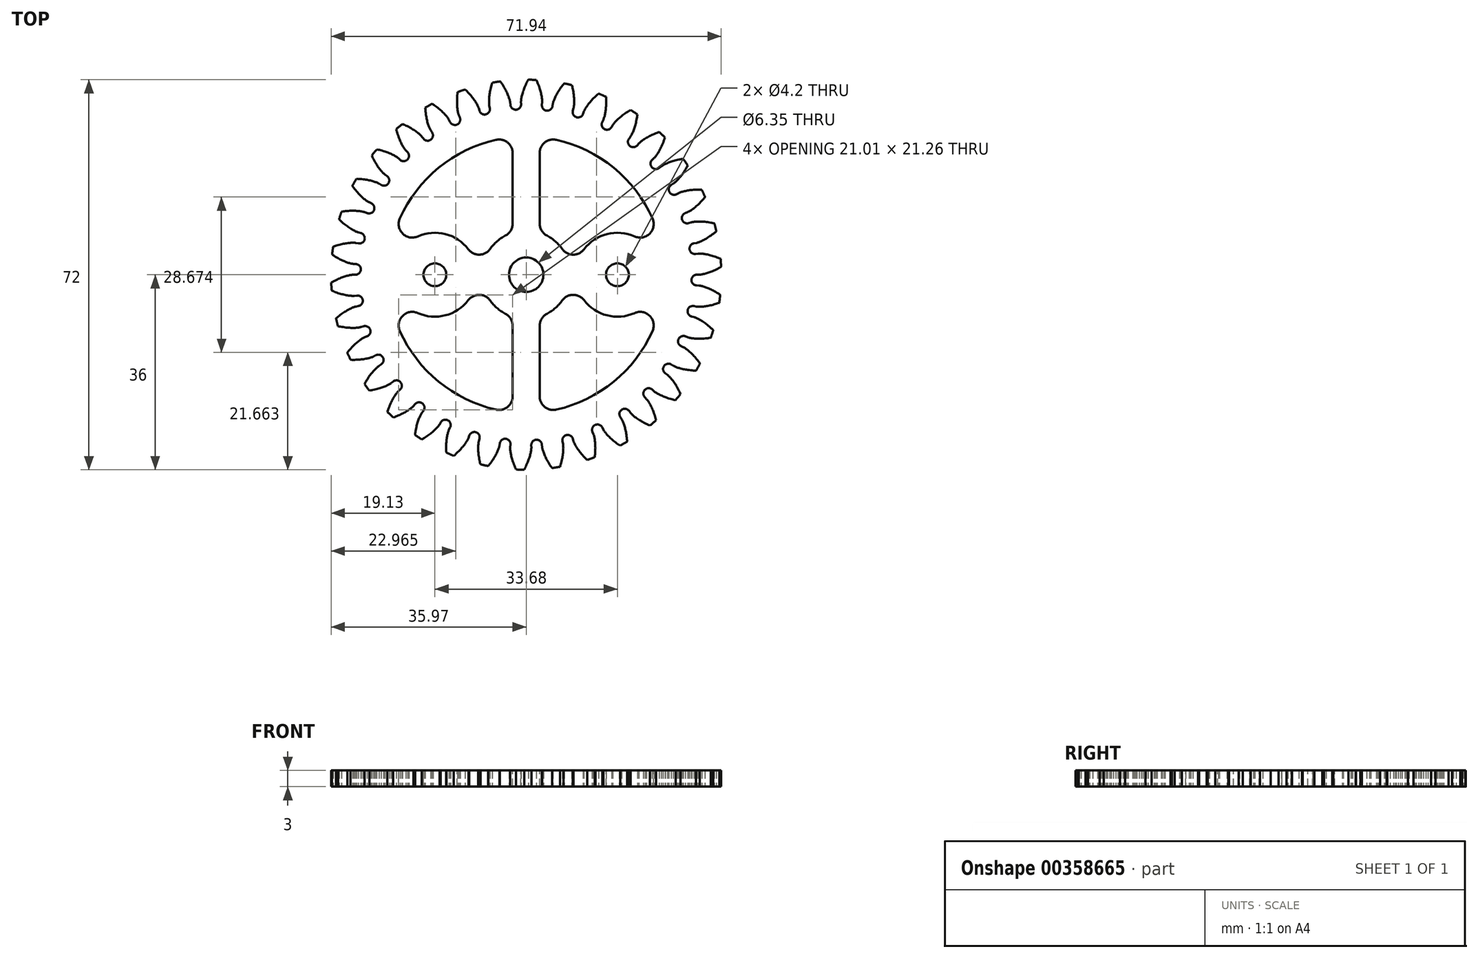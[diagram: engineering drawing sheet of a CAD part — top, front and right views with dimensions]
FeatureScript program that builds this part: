
annotation { "Feature Type Name" : "Feature", "Feature Type Description" : "" }
export const myFeature = defineFeature(function(context is Context, id is Id, definition is map)
    precondition{}
    {
        {
            assignVariable(context, id + "F0", {"name" : "T", "anyValue" : 34});
        }
        {
            assignVariable(context, id + "F1", {"name" : "SP", "anyValue" : 4});
        }
        {
            assignVariable(context, id + "F2", {"name" : "SF", "anyValue" : 2.5});
        }
        {
            var Q0;
            Q0=qCreatedBy(makeId("Top.planeOp"),FACE);
            var sketch = newSketch(context, id + "F3", { "sketchPlane" : qUnion([Q0])});
            skCircle(sketch, "E0", {"center": v(0, 0) * mm, "radius": 36 * mm});
            skCircle(sketch, "E1", {"center": v(0, 0) * mm, "radius": 34 * mm, "construction": true});
            skCircle(sketch, "E2", {"center": v(0, 0) * mm, "radius": 31.95 * mm, "construction": true});
            skCircle(sketch, "E3", {"center": v(0, 0) * mm, "radius": 31.5 * mm});
            skLineSegment(sketch, "E4", {"start": v(0, 0) * mm, "end": v(31.95, 0) * mm});
            skFitSpline(sketch, "E5", {"points": [v(31.95, 0) * mm, v(32, 0) * mm, v(32.14, 0.01) * mm, v(32.37, 0.05) * mm, v(32.7, 0.1) * mm, v(33.11, 0.21) * mm, v(33.61, 0.37) * mm, v(34.2, 0.58) * mm, v(34.85, 0.87) * mm, v(35.57, 1.23) * mm, v(36.35, 1.68) * mm], "startDerivative": vector(4.26, 0.15) * mm, "endDerivative": vector(16.12, 9.2) * mm});
            skLineSegment(sketch, "E6", {"start": v(0, 0) * mm, "end": v(35.98, -1.13) * mm, "construction": true});
            skLineSegment(sketch, "E7", {"start": v(0, 0) * mm, "end": v(34, 0.5) * mm, "construction": true});
            skFitSpline(sketch, "E8.MirrorCS", {"points": [v(31.89, -2) * mm, v(31.93, -2) * mm, v(32.08, -2.02) * mm, v(32.3, -2.07) * mm, v(32.63, -2.15) * mm, v(33.04, -2.28) * mm, v(33.52, -2.47) * mm, v(34.09, -2.72) * mm, v(34.72, -3.04) * mm, v(35.42, -3.45) * mm, v(36.18, -3.94) * mm], "startDerivative": vector(4.24, -0.42) * mm, "endDerivative": vector(15.51, -10.19) * mm});
            skLineSegment(sketch, "E9", {"start": v(0, 0) * mm, "end": v(31.89, -2) * mm});
            skSolve(sketch);
        }
        {
            var Q0;
            Q0=qCreatedBy(makeId("Top.planeOp"),FACE);
            var sketch = newSketch(context, id + "F4", { "sketchPlane" : qUnion([Q0])});
            skCircle(sketch, "E10", {"center": v(0, 0) * mm, "radius": 36 * mm});
            skSolve(sketch);
        }
        {
            var Q0;
            {var subQ0=sQuery(id+"F3.wireOp",EDGE,"E5");var subQ7=sQuery(id+"F3.wireOp",EDGE,"E0");var subQ8=makeQuery(id+"F3.imprint","INTERSECT",VERTEX,{"derivedFrom":[subQ7,subQ0]});Q0=makeQuery(id+"F3.imprint","IMPRINT",FACE,{"disambiguationData":[TD([[makeQuery(id+"F3.imprint","IMPRINT",EDGE,{"disambiguationData":[TD([[subQ8,1.0]])],"derivedFrom":subQ7}),1.0]])]});}
            extrude(context, id + "F5", {"entities" : qUnion([Q0]), "depth" : 6 * mm});
        }
        {
            var Q0;
            Q0=makeQuery(id+"F5.opExtrude","CAP_FACE",FACE,{"disambiguationData":[OSD([sQuery(id+"F3.wireOp",EDGE,"E0"),sQuery(id+"F3.wireOp",EDGE,"E3"),sQuery(id+"F3.wireOp",EDGE,"E4"),sQuery(id+"F3.wireOp",EDGE,"E5"),sQuery(id+"F3.wireOp",EDGE,"E8.MirrorCS"),sQuery(id+"F3.wireOp",EDGE,"E9")])],"isStart":true});
            var sketch = newSketch(context, id + "F6", { "sketchPlane" : qUnion([Q0])});
            skCircle(sketch, "E11", {"center": v(31.48, 0.99) * mm, "radius": 0.99 * mm});
            skSolve(sketch);
        }
        {
            var Q0;
            {var subQ1=makeQuery(id+"F5.opExtrude","CAP_EDGE",EDGE,{"disambiguationData":[OSD([sQuery(id+"F3.wireOp",EDGE,"E3")])],"isStart":true});Q0=makeQuery(id+"F6.imprint","IMPRINT",FACE,{"disambiguationData":[TD([[makeQuery(id+"F6.imprint","IMPRINT",EDGE,{"derivedFrom":subQ1}),-1.0]])]});}
            extrude(context, id + "F7", {"entities" : qUnion([Q0]), "operationType" : NewBodyOperationType.ADD, "oppositeDirection" : true, "depth" : 6 * mm});
        }
        {
            var Q0;
            Q0=makeQuery(id+"F4.imprint","IMPRINT",FACE,{"disambiguationData":[TD([[makeQuery(id+"F4.imprint","IMPRINT",EDGE,{"derivedFrom":sQuery(id+"F4.wireOp",EDGE,"E10")}),1.0]])]});
            extrude(context, id + "F8", {"entities" : qUnion([Q0]), "depth" : 3 * mm, "offsetDistance" : 25 * mm});
        }
        {
            var Q0;
            Q0=makeQuery(id+"F5.opExtrude","SWEPT_BODY",BODY,{"disambiguationData":[OSD([sQuery(id+"F3.wireOp",EDGE,"E0"),sQuery(id+"F3.wireOp",EDGE,"E3"),sQuery(id+"F3.wireOp",EDGE,"E4"),sQuery(id+"F3.wireOp",EDGE,"E5"),sQuery(id+"F3.wireOp",EDGE,"E8.MirrorCS"),sQuery(id+"F3.wireOp",EDGE,"E9")])]});
            var Q1;
            Q1=makeQuery(id+"F8.opExtrude","CAP_EDGE",EDGE,{"disambiguationData":[OSD([sQuery(id+"F4.wireOp",EDGE,"E10")])],"isStart":false});
            circularPattern(context, id + "F9", {"entities" : qUnion([Q0]), "axis" : qUnion([Q1]), "angle" : 360 * degree, "instanceCount" : getVariable(context, 'T'), "equalSpace" : true});
        }
        {
            var Q0;
            Q0=makeQuery(id+"F9.opPattern","COPY",BODY,{"derivedFrom":makeQuery(id+"F5.opExtrude","SWEPT_BODY",BODY,{"disambiguationData":[OSD([sQuery(id+"F3.wireOp",EDGE,"E0"),sQuery(id+"F3.wireOp",EDGE,"E3"),sQuery(id+"F3.wireOp",EDGE,"E4"),sQuery(id+"F3.wireOp",EDGE,"E5"),sQuery(id+"F3.wireOp",EDGE,"E8.MirrorCS"),sQuery(id+"F3.wireOp",EDGE,"E9")])]}),"instanceName":"5"});
            var Q1;
            Q1=makeQuery(id+"F9.opPattern","COPY",BODY,{"derivedFrom":makeQuery(id+"F5.opExtrude","SWEPT_BODY",BODY,{"disambiguationData":[OSD([sQuery(id+"F3.wireOp",EDGE,"E0"),sQuery(id+"F3.wireOp",EDGE,"E3"),sQuery(id+"F3.wireOp",EDGE,"E4"),sQuery(id+"F3.wireOp",EDGE,"E5"),sQuery(id+"F3.wireOp",EDGE,"E8.MirrorCS"),sQuery(id+"F3.wireOp",EDGE,"E9")])]}),"instanceName":"6"});
            var Q2;
            Q2=makeQuery(id+"F9.opPattern","COPY",BODY,{"derivedFrom":makeQuery(id+"F5.opExtrude","SWEPT_BODY",BODY,{"disambiguationData":[OSD([sQuery(id+"F3.wireOp",EDGE,"E0"),sQuery(id+"F3.wireOp",EDGE,"E3"),sQuery(id+"F3.wireOp",EDGE,"E4"),sQuery(id+"F3.wireOp",EDGE,"E5"),sQuery(id+"F3.wireOp",EDGE,"E8.MirrorCS"),sQuery(id+"F3.wireOp",EDGE,"E9")])]}),"instanceName":"7"});
            var Q3;
            Q3=makeQuery(id+"F9.opPattern","COPY",BODY,{"derivedFrom":makeQuery(id+"F5.opExtrude","SWEPT_BODY",BODY,{"disambiguationData":[OSD([sQuery(id+"F3.wireOp",EDGE,"E0"),sQuery(id+"F3.wireOp",EDGE,"E3"),sQuery(id+"F3.wireOp",EDGE,"E4"),sQuery(id+"F3.wireOp",EDGE,"E5"),sQuery(id+"F3.wireOp",EDGE,"E8.MirrorCS"),sQuery(id+"F3.wireOp",EDGE,"E9")])]}),"instanceName":"8"});
            var Q4;
            Q4=makeQuery(id+"F9.opPattern","COPY",BODY,{"derivedFrom":makeQuery(id+"F5.opExtrude","SWEPT_BODY",BODY,{"disambiguationData":[OSD([sQuery(id+"F3.wireOp",EDGE,"E0"),sQuery(id+"F3.wireOp",EDGE,"E3"),sQuery(id+"F3.wireOp",EDGE,"E4"),sQuery(id+"F3.wireOp",EDGE,"E5"),sQuery(id+"F3.wireOp",EDGE,"E8.MirrorCS"),sQuery(id+"F3.wireOp",EDGE,"E9")])]}),"instanceName":"9"});
            var Q5;
            Q5=makeQuery(id+"F9.opPattern","COPY",BODY,{"derivedFrom":makeQuery(id+"F5.opExtrude","SWEPT_BODY",BODY,{"disambiguationData":[OSD([sQuery(id+"F3.wireOp",EDGE,"E0"),sQuery(id+"F3.wireOp",EDGE,"E3"),sQuery(id+"F3.wireOp",EDGE,"E4"),sQuery(id+"F3.wireOp",EDGE,"E5"),sQuery(id+"F3.wireOp",EDGE,"E8.MirrorCS"),sQuery(id+"F3.wireOp",EDGE,"E9")])]}),"instanceName":"10"});
            var Q6;
            Q6=makeQuery(id+"F9.opPattern","COPY",BODY,{"derivedFrom":makeQuery(id+"F5.opExtrude","SWEPT_BODY",BODY,{"disambiguationData":[OSD([sQuery(id+"F3.wireOp",EDGE,"E0"),sQuery(id+"F3.wireOp",EDGE,"E3"),sQuery(id+"F3.wireOp",EDGE,"E4"),sQuery(id+"F3.wireOp",EDGE,"E5"),sQuery(id+"F3.wireOp",EDGE,"E8.MirrorCS"),sQuery(id+"F3.wireOp",EDGE,"E9")])]}),"instanceName":"11"});
            var Q7;
            Q7=makeQuery(id+"F9.opPattern","COPY",BODY,{"derivedFrom":makeQuery(id+"F5.opExtrude","SWEPT_BODY",BODY,{"disambiguationData":[OSD([sQuery(id+"F3.wireOp",EDGE,"E0"),sQuery(id+"F3.wireOp",EDGE,"E3"),sQuery(id+"F3.wireOp",EDGE,"E4"),sQuery(id+"F3.wireOp",EDGE,"E5"),sQuery(id+"F3.wireOp",EDGE,"E8.MirrorCS"),sQuery(id+"F3.wireOp",EDGE,"E9")])]}),"instanceName":"12"});
            var Q8;
            Q8=makeQuery(id+"F9.opPattern","COPY",BODY,{"derivedFrom":makeQuery(id+"F5.opExtrude","SWEPT_BODY",BODY,{"disambiguationData":[OSD([sQuery(id+"F3.wireOp",EDGE,"E0"),sQuery(id+"F3.wireOp",EDGE,"E3"),sQuery(id+"F3.wireOp",EDGE,"E4"),sQuery(id+"F3.wireOp",EDGE,"E5"),sQuery(id+"F3.wireOp",EDGE,"E8.MirrorCS"),sQuery(id+"F3.wireOp",EDGE,"E9")])]}),"instanceName":"13"});
            var Q9;
            Q9=makeQuery(id+"F9.opPattern","COPY",BODY,{"derivedFrom":makeQuery(id+"F5.opExtrude","SWEPT_BODY",BODY,{"disambiguationData":[OSD([sQuery(id+"F3.wireOp",EDGE,"E0"),sQuery(id+"F3.wireOp",EDGE,"E3"),sQuery(id+"F3.wireOp",EDGE,"E4"),sQuery(id+"F3.wireOp",EDGE,"E5"),sQuery(id+"F3.wireOp",EDGE,"E8.MirrorCS"),sQuery(id+"F3.wireOp",EDGE,"E9")])]}),"instanceName":"14"});
            var Q10;
            Q10=makeQuery(id+"F9.opPattern","COPY",BODY,{"derivedFrom":makeQuery(id+"F5.opExtrude","SWEPT_BODY",BODY,{"disambiguationData":[OSD([sQuery(id+"F3.wireOp",EDGE,"E0"),sQuery(id+"F3.wireOp",EDGE,"E3"),sQuery(id+"F3.wireOp",EDGE,"E4"),sQuery(id+"F3.wireOp",EDGE,"E5"),sQuery(id+"F3.wireOp",EDGE,"E8.MirrorCS"),sQuery(id+"F3.wireOp",EDGE,"E9")])]}),"instanceName":"15"});
            var Q11;
            Q11=makeQuery(id+"F9.opPattern","COPY",BODY,{"derivedFrom":makeQuery(id+"F5.opExtrude","SWEPT_BODY",BODY,{"disambiguationData":[OSD([sQuery(id+"F3.wireOp",EDGE,"E0"),sQuery(id+"F3.wireOp",EDGE,"E3"),sQuery(id+"F3.wireOp",EDGE,"E4"),sQuery(id+"F3.wireOp",EDGE,"E5"),sQuery(id+"F3.wireOp",EDGE,"E8.MirrorCS"),sQuery(id+"F3.wireOp",EDGE,"E9")])]}),"instanceName":"16"});
            var Q12;
            Q12=makeQuery(id+"F9.opPattern","COPY",BODY,{"derivedFrom":makeQuery(id+"F5.opExtrude","SWEPT_BODY",BODY,{"disambiguationData":[OSD([sQuery(id+"F3.wireOp",EDGE,"E0"),sQuery(id+"F3.wireOp",EDGE,"E3"),sQuery(id+"F3.wireOp",EDGE,"E4"),sQuery(id+"F3.wireOp",EDGE,"E5"),sQuery(id+"F3.wireOp",EDGE,"E8.MirrorCS"),sQuery(id+"F3.wireOp",EDGE,"E9")])]}),"instanceName":"17"});
            var Q13;
            Q13=makeQuery(id+"F9.opPattern","COPY",BODY,{"derivedFrom":makeQuery(id+"F5.opExtrude","SWEPT_BODY",BODY,{"disambiguationData":[OSD([sQuery(id+"F3.wireOp",EDGE,"E0"),sQuery(id+"F3.wireOp",EDGE,"E3"),sQuery(id+"F3.wireOp",EDGE,"E4"),sQuery(id+"F3.wireOp",EDGE,"E5"),sQuery(id+"F3.wireOp",EDGE,"E8.MirrorCS"),sQuery(id+"F3.wireOp",EDGE,"E9")])]}),"instanceName":"18"});
            var Q14;
            Q14=makeQuery(id+"F9.opPattern","COPY",BODY,{"derivedFrom":makeQuery(id+"F5.opExtrude","SWEPT_BODY",BODY,{"disambiguationData":[OSD([sQuery(id+"F3.wireOp",EDGE,"E0"),sQuery(id+"F3.wireOp",EDGE,"E3"),sQuery(id+"F3.wireOp",EDGE,"E4"),sQuery(id+"F3.wireOp",EDGE,"E5"),sQuery(id+"F3.wireOp",EDGE,"E8.MirrorCS"),sQuery(id+"F3.wireOp",EDGE,"E9")])]}),"instanceName":"19"});
            var Q15;
            Q15=makeQuery(id+"F9.opPattern","COPY",BODY,{"derivedFrom":makeQuery(id+"F5.opExtrude","SWEPT_BODY",BODY,{"disambiguationData":[OSD([sQuery(id+"F3.wireOp",EDGE,"E0"),sQuery(id+"F3.wireOp",EDGE,"E3"),sQuery(id+"F3.wireOp",EDGE,"E4"),sQuery(id+"F3.wireOp",EDGE,"E5"),sQuery(id+"F3.wireOp",EDGE,"E8.MirrorCS"),sQuery(id+"F3.wireOp",EDGE,"E9")])]}),"instanceName":"20"});
            var Q16;
            Q16=makeQuery(id+"F9.opPattern","COPY",BODY,{"derivedFrom":makeQuery(id+"F5.opExtrude","SWEPT_BODY",BODY,{"disambiguationData":[OSD([sQuery(id+"F3.wireOp",EDGE,"E0"),sQuery(id+"F3.wireOp",EDGE,"E3"),sQuery(id+"F3.wireOp",EDGE,"E4"),sQuery(id+"F3.wireOp",EDGE,"E5"),sQuery(id+"F3.wireOp",EDGE,"E8.MirrorCS"),sQuery(id+"F3.wireOp",EDGE,"E9")])]}),"instanceName":"21"});
            var Q17;
            Q17=makeQuery(id+"F9.opPattern","COPY",BODY,{"derivedFrom":makeQuery(id+"F5.opExtrude","SWEPT_BODY",BODY,{"disambiguationData":[OSD([sQuery(id+"F3.wireOp",EDGE,"E0"),sQuery(id+"F3.wireOp",EDGE,"E3"),sQuery(id+"F3.wireOp",EDGE,"E4"),sQuery(id+"F3.wireOp",EDGE,"E5"),sQuery(id+"F3.wireOp",EDGE,"E8.MirrorCS"),sQuery(id+"F3.wireOp",EDGE,"E9")])]}),"instanceName":"22"});
            var Q18;
            Q18=makeQuery(id+"F9.opPattern","COPY",BODY,{"derivedFrom":makeQuery(id+"F5.opExtrude","SWEPT_BODY",BODY,{"disambiguationData":[OSD([sQuery(id+"F3.wireOp",EDGE,"E0"),sQuery(id+"F3.wireOp",EDGE,"E3"),sQuery(id+"F3.wireOp",EDGE,"E4"),sQuery(id+"F3.wireOp",EDGE,"E5"),sQuery(id+"F3.wireOp",EDGE,"E8.MirrorCS"),sQuery(id+"F3.wireOp",EDGE,"E9")])]}),"instanceName":"23"});
            var Q19;
            Q19=makeQuery(id+"F9.opPattern","COPY",BODY,{"derivedFrom":makeQuery(id+"F5.opExtrude","SWEPT_BODY",BODY,{"disambiguationData":[OSD([sQuery(id+"F3.wireOp",EDGE,"E0"),sQuery(id+"F3.wireOp",EDGE,"E3"),sQuery(id+"F3.wireOp",EDGE,"E4"),sQuery(id+"F3.wireOp",EDGE,"E5"),sQuery(id+"F3.wireOp",EDGE,"E8.MirrorCS"),sQuery(id+"F3.wireOp",EDGE,"E9")])]}),"instanceName":"24"});
            var Q20;
            Q20=makeQuery(id+"F9.opPattern","COPY",BODY,{"derivedFrom":makeQuery(id+"F5.opExtrude","SWEPT_BODY",BODY,{"disambiguationData":[OSD([sQuery(id+"F3.wireOp",EDGE,"E0"),sQuery(id+"F3.wireOp",EDGE,"E3"),sQuery(id+"F3.wireOp",EDGE,"E4"),sQuery(id+"F3.wireOp",EDGE,"E5"),sQuery(id+"F3.wireOp",EDGE,"E8.MirrorCS"),sQuery(id+"F3.wireOp",EDGE,"E9")])]}),"instanceName":"25"});
            var Q21;
            Q21=makeQuery(id+"F9.opPattern","COPY",BODY,{"derivedFrom":makeQuery(id+"F5.opExtrude","SWEPT_BODY",BODY,{"disambiguationData":[OSD([sQuery(id+"F3.wireOp",EDGE,"E0"),sQuery(id+"F3.wireOp",EDGE,"E3"),sQuery(id+"F3.wireOp",EDGE,"E4"),sQuery(id+"F3.wireOp",EDGE,"E5"),sQuery(id+"F3.wireOp",EDGE,"E8.MirrorCS"),sQuery(id+"F3.wireOp",EDGE,"E9")])]}),"instanceName":"26"});
            var Q22;
            Q22=makeQuery(id+"F9.opPattern","COPY",BODY,{"derivedFrom":makeQuery(id+"F5.opExtrude","SWEPT_BODY",BODY,{"disambiguationData":[OSD([sQuery(id+"F3.wireOp",EDGE,"E0"),sQuery(id+"F3.wireOp",EDGE,"E3"),sQuery(id+"F3.wireOp",EDGE,"E4"),sQuery(id+"F3.wireOp",EDGE,"E5"),sQuery(id+"F3.wireOp",EDGE,"E8.MirrorCS"),sQuery(id+"F3.wireOp",EDGE,"E9")])]}),"instanceName":"27"});
            var Q23;
            Q23=makeQuery(id+"F9.opPattern","COPY",BODY,{"derivedFrom":makeQuery(id+"F5.opExtrude","SWEPT_BODY",BODY,{"disambiguationData":[OSD([sQuery(id+"F3.wireOp",EDGE,"E0"),sQuery(id+"F3.wireOp",EDGE,"E3"),sQuery(id+"F3.wireOp",EDGE,"E4"),sQuery(id+"F3.wireOp",EDGE,"E5"),sQuery(id+"F3.wireOp",EDGE,"E8.MirrorCS"),sQuery(id+"F3.wireOp",EDGE,"E9")])]}),"instanceName":"28"});
            var Q24;
            Q24=makeQuery(id+"F9.opPattern","COPY",BODY,{"derivedFrom":makeQuery(id+"F5.opExtrude","SWEPT_BODY",BODY,{"disambiguationData":[OSD([sQuery(id+"F3.wireOp",EDGE,"E0"),sQuery(id+"F3.wireOp",EDGE,"E3"),sQuery(id+"F3.wireOp",EDGE,"E4"),sQuery(id+"F3.wireOp",EDGE,"E5"),sQuery(id+"F3.wireOp",EDGE,"E8.MirrorCS"),sQuery(id+"F3.wireOp",EDGE,"E9")])]}),"instanceName":"29"});
            var Q25;
            Q25=makeQuery(id+"F5.opExtrude","SWEPT_BODY",BODY,{"disambiguationData":[OSD([sQuery(id+"F3.wireOp",EDGE,"E0"),sQuery(id+"F3.wireOp",EDGE,"E3"),sQuery(id+"F3.wireOp",EDGE,"E4"),sQuery(id+"F3.wireOp",EDGE,"E5"),sQuery(id+"F3.wireOp",EDGE,"E8.MirrorCS"),sQuery(id+"F3.wireOp",EDGE,"E9")])]});
            var Q26;
            Q26=makeQuery(id+"F9.opPattern","COPY",BODY,{"derivedFrom":makeQuery(id+"F5.opExtrude","SWEPT_BODY",BODY,{"disambiguationData":[OSD([sQuery(id+"F3.wireOp",EDGE,"E0"),sQuery(id+"F3.wireOp",EDGE,"E3"),sQuery(id+"F3.wireOp",EDGE,"E4"),sQuery(id+"F3.wireOp",EDGE,"E5"),sQuery(id+"F3.wireOp",EDGE,"E8.MirrorCS"),sQuery(id+"F3.wireOp",EDGE,"E9")])]}),"instanceName":"1"});
            var Q27;
            Q27=makeQuery(id+"F9.opPattern","COPY",BODY,{"derivedFrom":makeQuery(id+"F5.opExtrude","SWEPT_BODY",BODY,{"disambiguationData":[OSD([sQuery(id+"F3.wireOp",EDGE,"E0"),sQuery(id+"F3.wireOp",EDGE,"E3"),sQuery(id+"F3.wireOp",EDGE,"E4"),sQuery(id+"F3.wireOp",EDGE,"E5"),sQuery(id+"F3.wireOp",EDGE,"E8.MirrorCS"),sQuery(id+"F3.wireOp",EDGE,"E9")])]}),"instanceName":"2"});
            var Q28;
            Q28=makeQuery(id+"F9.opPattern","COPY",BODY,{"derivedFrom":makeQuery(id+"F5.opExtrude","SWEPT_BODY",BODY,{"disambiguationData":[OSD([sQuery(id+"F3.wireOp",EDGE,"E0"),sQuery(id+"F3.wireOp",EDGE,"E3"),sQuery(id+"F3.wireOp",EDGE,"E4"),sQuery(id+"F3.wireOp",EDGE,"E5"),sQuery(id+"F3.wireOp",EDGE,"E8.MirrorCS"),sQuery(id+"F3.wireOp",EDGE,"E9")])]}),"instanceName":"3"});
            var Q29;
            Q29=makeQuery(id+"F9.opPattern","COPY",BODY,{"derivedFrom":makeQuery(id+"F5.opExtrude","SWEPT_BODY",BODY,{"disambiguationData":[OSD([sQuery(id+"F3.wireOp",EDGE,"E0"),sQuery(id+"F3.wireOp",EDGE,"E3"),sQuery(id+"F3.wireOp",EDGE,"E4"),sQuery(id+"F3.wireOp",EDGE,"E5"),sQuery(id+"F3.wireOp",EDGE,"E8.MirrorCS"),sQuery(id+"F3.wireOp",EDGE,"E9")])]}),"instanceName":"4"});
            var Q30;
            Q30=makeQuery(id+"F9.opPattern","COPY",BODY,{"derivedFrom":makeQuery(id+"F5.opExtrude","SWEPT_BODY",BODY,{"disambiguationData":[OSD([sQuery(id+"F3.wireOp",EDGE,"E0"),sQuery(id+"F3.wireOp",EDGE,"E3"),sQuery(id+"F3.wireOp",EDGE,"E5"),sQuery(id+"F3.wireOp",EDGE,"E8.MirrorCS")])]}),"instanceName":"30"});
            var Q31;
            Q31=makeQuery(id+"F9.opPattern","COPY",BODY,{"derivedFrom":makeQuery(id+"F5.opExtrude","SWEPT_BODY",BODY,{"disambiguationData":[OSD([sQuery(id+"F3.wireOp",EDGE,"E0"),sQuery(id+"F3.wireOp",EDGE,"E3"),sQuery(id+"F3.wireOp",EDGE,"E5"),sQuery(id+"F3.wireOp",EDGE,"E8.MirrorCS")])]}),"instanceName":"31"});
            var Q32;
            Q32=makeQuery(id+"F9.opPattern","COPY",BODY,{"derivedFrom":makeQuery(id+"F5.opExtrude","SWEPT_BODY",BODY,{"disambiguationData":[OSD([sQuery(id+"F3.wireOp",EDGE,"E0"),sQuery(id+"F3.wireOp",EDGE,"E3"),sQuery(id+"F3.wireOp",EDGE,"E5"),sQuery(id+"F3.wireOp",EDGE,"E8.MirrorCS")])]}),"instanceName":"32"});
            var Q33;
            Q33=makeQuery(id+"F9.opPattern","COPY",BODY,{"derivedFrom":makeQuery(id+"F5.opExtrude","SWEPT_BODY",BODY,{"disambiguationData":[OSD([sQuery(id+"F3.wireOp",EDGE,"E0"),sQuery(id+"F3.wireOp",EDGE,"E3"),sQuery(id+"F3.wireOp",EDGE,"E5"),sQuery(id+"F3.wireOp",EDGE,"E8.MirrorCS")])]}),"instanceName":"33"});
            var Q34;
            Q34=makeQuery(id+"F9.opPattern","COPY",BODY,{"derivedFrom":makeQuery(id+"F5.opExtrude","SWEPT_BODY",BODY,{"disambiguationData":[OSD([sQuery(id+"F3.wireOp",EDGE,"E0"),sQuery(id+"F3.wireOp",EDGE,"E3"),sQuery(id+"F3.wireOp",EDGE,"E5"),sQuery(id+"F3.wireOp",EDGE,"E8.MirrorCS")])]}),"instanceName":"34"});
            var Q35;
            Q35=makeQuery(id+"F9.opPattern","COPY",BODY,{"derivedFrom":makeQuery(id+"F5.opExtrude","SWEPT_BODY",BODY,{"disambiguationData":[OSD([sQuery(id+"F3.wireOp",EDGE,"E0"),sQuery(id+"F3.wireOp",EDGE,"E3"),sQuery(id+"F3.wireOp",EDGE,"E5"),sQuery(id+"F3.wireOp",EDGE,"E8.MirrorCS")])]}),"instanceName":"35"});
            var Q36;
            Q36=makeQuery(id+"F9.opPattern","COPY",BODY,{"derivedFrom":makeQuery(id+"F5.opExtrude","SWEPT_BODY",BODY,{"disambiguationData":[OSD([sQuery(id+"F3.wireOp",EDGE,"E0"),sQuery(id+"F3.wireOp",EDGE,"E3"),sQuery(id+"F3.wireOp",EDGE,"E5"),sQuery(id+"F3.wireOp",EDGE,"E8.MirrorCS")])]}),"instanceName":"36"});
            var Q37;
            Q37=makeQuery(id+"F9.opPattern","COPY",BODY,{"derivedFrom":makeQuery(id+"F5.opExtrude","SWEPT_BODY",BODY,{"disambiguationData":[OSD([sQuery(id+"F3.wireOp",EDGE,"E0"),sQuery(id+"F3.wireOp",EDGE,"E3"),sQuery(id+"F3.wireOp",EDGE,"E5"),sQuery(id+"F3.wireOp",EDGE,"E8.MirrorCS")])]}),"instanceName":"37"});
            var Q38;
            Q38=makeQuery(id+"F9.opPattern","COPY",BODY,{"derivedFrom":makeQuery(id+"F5.opExtrude","SWEPT_BODY",BODY,{"disambiguationData":[OSD([sQuery(id+"F3.wireOp",EDGE,"E0"),sQuery(id+"F3.wireOp",EDGE,"E3"),sQuery(id+"F3.wireOp",EDGE,"E5"),sQuery(id+"F3.wireOp",EDGE,"E8.MirrorCS")])]}),"instanceName":"38"});
            var Q39;
            Q39=makeQuery(id+"F9.opPattern","COPY",BODY,{"derivedFrom":makeQuery(id+"F5.opExtrude","SWEPT_BODY",BODY,{"disambiguationData":[OSD([sQuery(id+"F3.wireOp",EDGE,"E0"),sQuery(id+"F3.wireOp",EDGE,"E3"),sQuery(id+"F3.wireOp",EDGE,"E5"),sQuery(id+"F3.wireOp",EDGE,"E8.MirrorCS")])]}),"instanceName":"39"});
            var Q40;
            Q40=makeQuery(id+"F9.opPattern","COPY",BODY,{"derivedFrom":makeQuery(id+"F5.opExtrude","SWEPT_BODY",BODY,{"disambiguationData":[OSD([sQuery(id+"F3.wireOp",EDGE,"E0"),sQuery(id+"F3.wireOp",EDGE,"E3"),sQuery(id+"F3.wireOp",EDGE,"E5"),sQuery(id+"F3.wireOp",EDGE,"E8.MirrorCS")])]}),"instanceName":"40"});
            var Q41;
            Q41=makeQuery(id+"F9.opPattern","COPY",BODY,{"derivedFrom":makeQuery(id+"F5.opExtrude","SWEPT_BODY",BODY,{"disambiguationData":[OSD([sQuery(id+"F3.wireOp",EDGE,"E0"),sQuery(id+"F3.wireOp",EDGE,"E3"),sQuery(id+"F3.wireOp",EDGE,"E5"),sQuery(id+"F3.wireOp",EDGE,"E8.MirrorCS")])]}),"instanceName":"41"});
            var Q42;
            Q42=makeQuery(id+"F9.opPattern","COPY",BODY,{"derivedFrom":makeQuery(id+"F5.opExtrude","SWEPT_BODY",BODY,{"disambiguationData":[OSD([sQuery(id+"F3.wireOp",EDGE,"E0"),sQuery(id+"F3.wireOp",EDGE,"E3"),sQuery(id+"F3.wireOp",EDGE,"E5"),sQuery(id+"F3.wireOp",EDGE,"E8.MirrorCS")])]}),"instanceName":"42"});
            var Q43;
            Q43=makeQuery(id+"F9.opPattern","COPY",BODY,{"derivedFrom":makeQuery(id+"F5.opExtrude","SWEPT_BODY",BODY,{"disambiguationData":[OSD([sQuery(id+"F3.wireOp",EDGE,"E0"),sQuery(id+"F3.wireOp",EDGE,"E3"),sQuery(id+"F3.wireOp",EDGE,"E5"),sQuery(id+"F3.wireOp",EDGE,"E8.MirrorCS")])]}),"instanceName":"43"});
            var Q44;
            Q44=makeQuery(id+"F9.opPattern","COPY",BODY,{"derivedFrom":makeQuery(id+"F5.opExtrude","SWEPT_BODY",BODY,{"disambiguationData":[OSD([sQuery(id+"F3.wireOp",EDGE,"E0"),sQuery(id+"F3.wireOp",EDGE,"E3"),sQuery(id+"F3.wireOp",EDGE,"E5"),sQuery(id+"F3.wireOp",EDGE,"E8.MirrorCS")])]}),"instanceName":"44"});
            var Q45;
            Q45=makeQuery(id+"F9.opPattern","COPY",BODY,{"derivedFrom":makeQuery(id+"F5.opExtrude","SWEPT_BODY",BODY,{"disambiguationData":[OSD([sQuery(id+"F3.wireOp",EDGE,"E0"),sQuery(id+"F3.wireOp",EDGE,"E3"),sQuery(id+"F3.wireOp",EDGE,"E5"),sQuery(id+"F3.wireOp",EDGE,"E8.MirrorCS")])]}),"instanceName":"45"});
            var Q46;
            Q46=makeQuery(id+"F9.opPattern","COPY",BODY,{"derivedFrom":makeQuery(id+"F5.opExtrude","SWEPT_BODY",BODY,{"disambiguationData":[OSD([sQuery(id+"F3.wireOp",EDGE,"E0"),sQuery(id+"F3.wireOp",EDGE,"E3"),sQuery(id+"F3.wireOp",EDGE,"E5"),sQuery(id+"F3.wireOp",EDGE,"E8.MirrorCS")])]}),"instanceName":"46"});
            var Q47;
            Q47=makeQuery(id+"F9.opPattern","COPY",BODY,{"derivedFrom":makeQuery(id+"F5.opExtrude","SWEPT_BODY",BODY,{"disambiguationData":[OSD([sQuery(id+"F3.wireOp",EDGE,"E0"),sQuery(id+"F3.wireOp",EDGE,"E3"),sQuery(id+"F3.wireOp",EDGE,"E5"),sQuery(id+"F3.wireOp",EDGE,"E8.MirrorCS")])]}),"instanceName":"47"});
            var Q48;
            Q48=makeQuery(id+"F9.opPattern","COPY",BODY,{"derivedFrom":makeQuery(id+"F5.opExtrude","SWEPT_BODY",BODY,{"disambiguationData":[OSD([sQuery(id+"F3.wireOp",EDGE,"E0"),sQuery(id+"F3.wireOp",EDGE,"E3"),sQuery(id+"F3.wireOp",EDGE,"E5"),sQuery(id+"F3.wireOp",EDGE,"E8.MirrorCS")])]}),"instanceName":"48"});
            var Q49;
            Q49=makeQuery(id+"F9.opPattern","COPY",BODY,{"derivedFrom":makeQuery(id+"F5.opExtrude","SWEPT_BODY",BODY,{"disambiguationData":[OSD([sQuery(id+"F3.wireOp",EDGE,"E0"),sQuery(id+"F3.wireOp",EDGE,"E3"),sQuery(id+"F3.wireOp",EDGE,"E5"),sQuery(id+"F3.wireOp",EDGE,"E8.MirrorCS")])]}),"instanceName":"49"});
            var Q50;
            Q50=makeQuery(id+"F9.opPattern","COPY",BODY,{"derivedFrom":makeQuery(id+"F5.opExtrude","SWEPT_BODY",BODY,{"disambiguationData":[OSD([sQuery(id+"F3.wireOp",EDGE,"E0"),sQuery(id+"F3.wireOp",EDGE,"E3"),sQuery(id+"F3.wireOp",EDGE,"E5"),sQuery(id+"F3.wireOp",EDGE,"E8.MirrorCS")])]}),"instanceName":"50"});
            var Q51;
            Q51=makeQuery(id+"F9.opPattern","COPY",BODY,{"derivedFrom":makeQuery(id+"F5.opExtrude","SWEPT_BODY",BODY,{"disambiguationData":[OSD([sQuery(id+"F3.wireOp",EDGE,"E0"),sQuery(id+"F3.wireOp",EDGE,"E3"),sQuery(id+"F3.wireOp",EDGE,"E5"),sQuery(id+"F3.wireOp",EDGE,"E8.MirrorCS")])]}),"instanceName":"51"});
            var Q52;
            Q52=makeQuery(id+"F9.opPattern","COPY",BODY,{"derivedFrom":makeQuery(id+"F5.opExtrude","SWEPT_BODY",BODY,{"disambiguationData":[OSD([sQuery(id+"F3.wireOp",EDGE,"E0"),sQuery(id+"F3.wireOp",EDGE,"E3"),sQuery(id+"F3.wireOp",EDGE,"E5"),sQuery(id+"F3.wireOp",EDGE,"E8.MirrorCS")])]}),"instanceName":"52"});
            var Q53;
            Q53=makeQuery(id+"F9.opPattern","COPY",BODY,{"derivedFrom":makeQuery(id+"F5.opExtrude","SWEPT_BODY",BODY,{"disambiguationData":[OSD([sQuery(id+"F3.wireOp",EDGE,"E0"),sQuery(id+"F3.wireOp",EDGE,"E3"),sQuery(id+"F3.wireOp",EDGE,"E5"),sQuery(id+"F3.wireOp",EDGE,"E8.MirrorCS")])]}),"instanceName":"53"});
            var Q54;
            Q54=makeQuery(id+"F9.opPattern","COPY",BODY,{"derivedFrom":makeQuery(id+"F5.opExtrude","SWEPT_BODY",BODY,{"disambiguationData":[OSD([sQuery(id+"F3.wireOp",EDGE,"E0"),sQuery(id+"F3.wireOp",EDGE,"E3"),sQuery(id+"F3.wireOp",EDGE,"E5"),sQuery(id+"F3.wireOp",EDGE,"E8.MirrorCS")])]}),"instanceName":"54"});
            var Q55;
            Q55=makeQuery(id+"F9.opPattern","COPY",BODY,{"derivedFrom":makeQuery(id+"F5.opExtrude","SWEPT_BODY",BODY,{"disambiguationData":[OSD([sQuery(id+"F3.wireOp",EDGE,"E0"),sQuery(id+"F3.wireOp",EDGE,"E3"),sQuery(id+"F3.wireOp",EDGE,"E5"),sQuery(id+"F3.wireOp",EDGE,"E8.MirrorCS")])]}),"instanceName":"55"});
            var Q56;
            Q56=makeQuery(id+"F9.opPattern","COPY",BODY,{"derivedFrom":makeQuery(id+"F5.opExtrude","SWEPT_BODY",BODY,{"disambiguationData":[OSD([sQuery(id+"F3.wireOp",EDGE,"E0"),sQuery(id+"F3.wireOp",EDGE,"E3"),sQuery(id+"F3.wireOp",EDGE,"E5"),sQuery(id+"F3.wireOp",EDGE,"E8.MirrorCS")])]}),"instanceName":"56"});
            var Q57;
            Q57=makeQuery(id+"F9.opPattern","COPY",BODY,{"derivedFrom":makeQuery(id+"F5.opExtrude","SWEPT_BODY",BODY,{"disambiguationData":[OSD([sQuery(id+"F3.wireOp",EDGE,"E0"),sQuery(id+"F3.wireOp",EDGE,"E3"),sQuery(id+"F3.wireOp",EDGE,"E5"),sQuery(id+"F3.wireOp",EDGE,"E8.MirrorCS")])]}),"instanceName":"57"});
            var Q58;
            Q58=makeQuery(id+"F9.opPattern","COPY",BODY,{"derivedFrom":makeQuery(id+"F5.opExtrude","SWEPT_BODY",BODY,{"disambiguationData":[OSD([sQuery(id+"F3.wireOp",EDGE,"E0"),sQuery(id+"F3.wireOp",EDGE,"E3"),sQuery(id+"F3.wireOp",EDGE,"E5"),sQuery(id+"F3.wireOp",EDGE,"E8.MirrorCS")])]}),"instanceName":"58"});
            var Q59;
            Q59=makeQuery(id+"F9.opPattern","COPY",BODY,{"derivedFrom":makeQuery(id+"F5.opExtrude","SWEPT_BODY",BODY,{"disambiguationData":[OSD([sQuery(id+"F3.wireOp",EDGE,"E0"),sQuery(id+"F3.wireOp",EDGE,"E3"),sQuery(id+"F3.wireOp",EDGE,"E5"),sQuery(id+"F3.wireOp",EDGE,"E8.MirrorCS")])]}),"instanceName":"59"});
            var Q60;
            Q60=makeQuery(id+"F9.opPattern","COPY",BODY,{"derivedFrom":makeQuery(id+"F5.opExtrude","SWEPT_BODY",BODY,{"disambiguationData":[OSD([sQuery(id+"F3.wireOp",EDGE,"E0"),sQuery(id+"F3.wireOp",EDGE,"E3"),sQuery(id+"F3.wireOp",EDGE,"E5"),sQuery(id+"F3.wireOp",EDGE,"E8.MirrorCS")])]}),"instanceName":"60"});
            var Q61;
            Q61=makeQuery(id+"F9.opPattern","COPY",BODY,{"derivedFrom":makeQuery(id+"F5.opExtrude","SWEPT_BODY",BODY,{"disambiguationData":[OSD([sQuery(id+"F3.wireOp",EDGE,"E0"),sQuery(id+"F3.wireOp",EDGE,"E3"),sQuery(id+"F3.wireOp",EDGE,"E5"),sQuery(id+"F3.wireOp",EDGE,"E8.MirrorCS")])]}),"instanceName":"61"});
            var Q62;
            Q62=makeQuery(id+"F9.opPattern","COPY",BODY,{"derivedFrom":makeQuery(id+"F5.opExtrude","SWEPT_BODY",BODY,{"disambiguationData":[OSD([sQuery(id+"F3.wireOp",EDGE,"E0"),sQuery(id+"F3.wireOp",EDGE,"E3"),sQuery(id+"F3.wireOp",EDGE,"E5"),sQuery(id+"F3.wireOp",EDGE,"E8.MirrorCS")])]}),"instanceName":"62"});
            var Q63;
            Q63=makeQuery(id+"F9.opPattern","COPY",BODY,{"derivedFrom":makeQuery(id+"F5.opExtrude","SWEPT_BODY",BODY,{"disambiguationData":[OSD([sQuery(id+"F3.wireOp",EDGE,"E0"),sQuery(id+"F3.wireOp",EDGE,"E3"),sQuery(id+"F3.wireOp",EDGE,"E5"),sQuery(id+"F3.wireOp",EDGE,"E8.MirrorCS")])]}),"instanceName":"63"});
            var Q64;
            Q64=makeQuery(id+"F9.opPattern","COPY",BODY,{"derivedFrom":makeQuery(id+"F5.opExtrude","SWEPT_BODY",BODY,{"disambiguationData":[OSD([sQuery(id+"F3.wireOp",EDGE,"E0"),sQuery(id+"F3.wireOp",EDGE,"E3"),sQuery(id+"F3.wireOp",EDGE,"E5"),sQuery(id+"F3.wireOp",EDGE,"E8.MirrorCS")])]}),"instanceName":"64"});
            var Q65;
            Q65=makeQuery(id+"F9.opPattern","COPY",BODY,{"derivedFrom":makeQuery(id+"F5.opExtrude","SWEPT_BODY",BODY,{"disambiguationData":[OSD([sQuery(id+"F3.wireOp",EDGE,"E0"),sQuery(id+"F3.wireOp",EDGE,"E3"),sQuery(id+"F3.wireOp",EDGE,"E5"),sQuery(id+"F3.wireOp",EDGE,"E8.MirrorCS")])]}),"instanceName":"65"});
            var Q66;
            Q66=makeQuery(id+"F9.opPattern","COPY",BODY,{"derivedFrom":makeQuery(id+"F5.opExtrude","SWEPT_BODY",BODY,{"disambiguationData":[OSD([sQuery(id+"F3.wireOp",EDGE,"E0"),sQuery(id+"F3.wireOp",EDGE,"E3"),sQuery(id+"F3.wireOp",EDGE,"E5"),sQuery(id+"F3.wireOp",EDGE,"E8.MirrorCS")])]}),"instanceName":"66"});
            var Q67;
            Q67=makeQuery(id+"F9.opPattern","COPY",BODY,{"derivedFrom":makeQuery(id+"F5.opExtrude","SWEPT_BODY",BODY,{"disambiguationData":[OSD([sQuery(id+"F3.wireOp",EDGE,"E0"),sQuery(id+"F3.wireOp",EDGE,"E3"),sQuery(id+"F3.wireOp",EDGE,"E5"),sQuery(id+"F3.wireOp",EDGE,"E8.MirrorCS")])]}),"instanceName":"67"});
            var Q68;
            Q68=makeQuery(id+"F9.opPattern","COPY",BODY,{"derivedFrom":makeQuery(id+"F5.opExtrude","SWEPT_BODY",BODY,{"disambiguationData":[OSD([sQuery(id+"F3.wireOp",EDGE,"E0"),sQuery(id+"F3.wireOp",EDGE,"E3"),sQuery(id+"F3.wireOp",EDGE,"E5"),sQuery(id+"F3.wireOp",EDGE,"E8.MirrorCS")])]}),"instanceName":"68"});
            var Q69;
            Q69=makeQuery(id+"F9.opPattern","COPY",BODY,{"derivedFrom":makeQuery(id+"F5.opExtrude","SWEPT_BODY",BODY,{"disambiguationData":[OSD([sQuery(id+"F3.wireOp",EDGE,"E0"),sQuery(id+"F3.wireOp",EDGE,"E3"),sQuery(id+"F3.wireOp",EDGE,"E5"),sQuery(id+"F3.wireOp",EDGE,"E8.MirrorCS")])]}),"instanceName":"69"});
            var Q70;
            Q70=makeQuery(id+"F9.opPattern","COPY",BODY,{"derivedFrom":makeQuery(id+"F5.opExtrude","SWEPT_BODY",BODY,{"disambiguationData":[OSD([sQuery(id+"F3.wireOp",EDGE,"E0"),sQuery(id+"F3.wireOp",EDGE,"E3"),sQuery(id+"F3.wireOp",EDGE,"E5"),sQuery(id+"F3.wireOp",EDGE,"E8.MirrorCS")])]}),"instanceName":"70"});
            var Q71;
            Q71=makeQuery(id+"F9.opPattern","COPY",BODY,{"derivedFrom":makeQuery(id+"F5.opExtrude","SWEPT_BODY",BODY,{"disambiguationData":[OSD([sQuery(id+"F3.wireOp",EDGE,"E0"),sQuery(id+"F3.wireOp",EDGE,"E3"),sQuery(id+"F3.wireOp",EDGE,"E5"),sQuery(id+"F3.wireOp",EDGE,"E8.MirrorCS")])]}),"instanceName":"71"});
            var Q72;
            Q72=makeQuery(id+"F9.opPattern","COPY",BODY,{"derivedFrom":makeQuery(id+"F5.opExtrude","SWEPT_BODY",BODY,{"disambiguationData":[OSD([sQuery(id+"F3.wireOp",EDGE,"E0"),sQuery(id+"F3.wireOp",EDGE,"E3"),sQuery(id+"F3.wireOp",EDGE,"E5"),sQuery(id+"F3.wireOp",EDGE,"E8.MirrorCS")])]}),"instanceName":"72"});
            var Q73;
            Q73=makeQuery(id+"F9.opPattern","COPY",BODY,{"derivedFrom":makeQuery(id+"F5.opExtrude","SWEPT_BODY",BODY,{"disambiguationData":[OSD([sQuery(id+"F3.wireOp",EDGE,"E0"),sQuery(id+"F3.wireOp",EDGE,"E3"),sQuery(id+"F3.wireOp",EDGE,"E5"),sQuery(id+"F3.wireOp",EDGE,"E8.MirrorCS")])]}),"instanceName":"73"});
            var Q74;
            Q74=makeQuery(id+"F9.opPattern","COPY",BODY,{"derivedFrom":makeQuery(id+"F5.opExtrude","SWEPT_BODY",BODY,{"disambiguationData":[OSD([sQuery(id+"F3.wireOp",EDGE,"E0"),sQuery(id+"F3.wireOp",EDGE,"E3"),sQuery(id+"F3.wireOp",EDGE,"E5"),sQuery(id+"F3.wireOp",EDGE,"E8.MirrorCS")])]}),"instanceName":"74"});
            var Q75;
            Q75=makeQuery(id+"F9.opPattern","COPY",BODY,{"derivedFrom":makeQuery(id+"F5.opExtrude","SWEPT_BODY",BODY,{"disambiguationData":[OSD([sQuery(id+"F3.wireOp",EDGE,"E0"),sQuery(id+"F3.wireOp",EDGE,"E3"),sQuery(id+"F3.wireOp",EDGE,"E5"),sQuery(id+"F3.wireOp",EDGE,"E8.MirrorCS")])]}),"instanceName":"75"});
            var Q76;
            Q76=makeQuery(id+"F9.opPattern","COPY",BODY,{"derivedFrom":makeQuery(id+"F5.opExtrude","SWEPT_BODY",BODY,{"disambiguationData":[OSD([sQuery(id+"F3.wireOp",EDGE,"E0"),sQuery(id+"F3.wireOp",EDGE,"E3"),sQuery(id+"F3.wireOp",EDGE,"E5"),sQuery(id+"F3.wireOp",EDGE,"E8.MirrorCS")])]}),"instanceName":"76"});
            var Q77;
            Q77=makeQuery(id+"F9.opPattern","COPY",BODY,{"derivedFrom":makeQuery(id+"F5.opExtrude","SWEPT_BODY",BODY,{"disambiguationData":[OSD([sQuery(id+"F3.wireOp",EDGE,"E0"),sQuery(id+"F3.wireOp",EDGE,"E3"),sQuery(id+"F3.wireOp",EDGE,"E5"),sQuery(id+"F3.wireOp",EDGE,"E8.MirrorCS")])]}),"instanceName":"77"});
            var Q78;
            Q78=makeQuery(id+"F9.opPattern","COPY",BODY,{"derivedFrom":makeQuery(id+"F5.opExtrude","SWEPT_BODY",BODY,{"disambiguationData":[OSD([sQuery(id+"F3.wireOp",EDGE,"E0"),sQuery(id+"F3.wireOp",EDGE,"E3"),sQuery(id+"F3.wireOp",EDGE,"E5"),sQuery(id+"F3.wireOp",EDGE,"E8.MirrorCS")])]}),"instanceName":"78"});
            var Q79;
            Q79=makeQuery(id+"F9.opPattern","COPY",BODY,{"derivedFrom":makeQuery(id+"F5.opExtrude","SWEPT_BODY",BODY,{"disambiguationData":[OSD([sQuery(id+"F3.wireOp",EDGE,"E0"),sQuery(id+"F3.wireOp",EDGE,"E3"),sQuery(id+"F3.wireOp",EDGE,"E5"),sQuery(id+"F3.wireOp",EDGE,"E8.MirrorCS")])]}),"instanceName":"79"});
            var Q80;
            Q80=makeQuery(id+"F9.opPattern","COPY",BODY,{"derivedFrom":makeQuery(id+"F5.opExtrude","SWEPT_BODY",BODY,{"disambiguationData":[OSD([sQuery(id+"F3.wireOp",EDGE,"E0"),sQuery(id+"F3.wireOp",EDGE,"E3"),sQuery(id+"F3.wireOp",EDGE,"E5"),sQuery(id+"F3.wireOp",EDGE,"E8.MirrorCS")])]}),"instanceName":"80"});
            var Q81;
            Q81=makeQuery(id+"F9.opPattern","COPY",BODY,{"derivedFrom":makeQuery(id+"F5.opExtrude","SWEPT_BODY",BODY,{"disambiguationData":[OSD([sQuery(id+"F3.wireOp",EDGE,"E0"),sQuery(id+"F3.wireOp",EDGE,"E3"),sQuery(id+"F3.wireOp",EDGE,"E5"),sQuery(id+"F3.wireOp",EDGE,"E8.MirrorCS")])]}),"instanceName":"81"});
            var Q82;
            Q82=makeQuery(id+"F9.opPattern","COPY",BODY,{"derivedFrom":makeQuery(id+"F5.opExtrude","SWEPT_BODY",BODY,{"disambiguationData":[OSD([sQuery(id+"F3.wireOp",EDGE,"E0"),sQuery(id+"F3.wireOp",EDGE,"E3"),sQuery(id+"F3.wireOp",EDGE,"E5"),sQuery(id+"F3.wireOp",EDGE,"E8.MirrorCS")])]}),"instanceName":"82"});
            var Q83;
            Q83=makeQuery(id+"F9.opPattern","COPY",BODY,{"derivedFrom":makeQuery(id+"F5.opExtrude","SWEPT_BODY",BODY,{"disambiguationData":[OSD([sQuery(id+"F3.wireOp",EDGE,"E0"),sQuery(id+"F3.wireOp",EDGE,"E3"),sQuery(id+"F3.wireOp",EDGE,"E5"),sQuery(id+"F3.wireOp",EDGE,"E8.MirrorCS")])]}),"instanceName":"83"});
            var Q84;
            Q84=makeQuery(id+"F9.opPattern","COPY",BODY,{"derivedFrom":makeQuery(id+"F5.opExtrude","SWEPT_BODY",BODY,{"disambiguationData":[OSD([sQuery(id+"F3.wireOp",EDGE,"E0"),sQuery(id+"F3.wireOp",EDGE,"E3"),sQuery(id+"F3.wireOp",EDGE,"E5"),sQuery(id+"F3.wireOp",EDGE,"E8.MirrorCS")])]}),"instanceName":"84"});
            var Q85;
            Q85=makeQuery(id+"F9.opPattern","COPY",BODY,{"derivedFrom":makeQuery(id+"F5.opExtrude","SWEPT_BODY",BODY,{"disambiguationData":[OSD([sQuery(id+"F3.wireOp",EDGE,"E0"),sQuery(id+"F3.wireOp",EDGE,"E3"),sQuery(id+"F3.wireOp",EDGE,"E5"),sQuery(id+"F3.wireOp",EDGE,"E8.MirrorCS")])]}),"instanceName":"85"});
            var Q86;
            Q86=makeQuery(id+"F9.opPattern","COPY",BODY,{"derivedFrom":makeQuery(id+"F5.opExtrude","SWEPT_BODY",BODY,{"disambiguationData":[OSD([sQuery(id+"F3.wireOp",EDGE,"E0"),sQuery(id+"F3.wireOp",EDGE,"E3"),sQuery(id+"F3.wireOp",EDGE,"E5"),sQuery(id+"F3.wireOp",EDGE,"E8.MirrorCS")])]}),"instanceName":"86"});
            var Q87;
            Q87=makeQuery(id+"F9.opPattern","COPY",BODY,{"derivedFrom":makeQuery(id+"F5.opExtrude","SWEPT_BODY",BODY,{"disambiguationData":[OSD([sQuery(id+"F3.wireOp",EDGE,"E0"),sQuery(id+"F3.wireOp",EDGE,"E3"),sQuery(id+"F3.wireOp",EDGE,"E5"),sQuery(id+"F3.wireOp",EDGE,"E8.MirrorCS")])]}),"instanceName":"87"});
            var Q88;
            Q88=makeQuery(id+"F9.opPattern","COPY",BODY,{"derivedFrom":makeQuery(id+"F5.opExtrude","SWEPT_BODY",BODY,{"disambiguationData":[OSD([sQuery(id+"F3.wireOp",EDGE,"E0"),sQuery(id+"F3.wireOp",EDGE,"E3"),sQuery(id+"F3.wireOp",EDGE,"E5"),sQuery(id+"F3.wireOp",EDGE,"E8.MirrorCS")])]}),"instanceName":"88"});
            var Q89;
            Q89=makeQuery(id+"F9.opPattern","COPY",BODY,{"derivedFrom":makeQuery(id+"F5.opExtrude","SWEPT_BODY",BODY,{"disambiguationData":[OSD([sQuery(id+"F3.wireOp",EDGE,"E0"),sQuery(id+"F3.wireOp",EDGE,"E3"),sQuery(id+"F3.wireOp",EDGE,"E5"),sQuery(id+"F3.wireOp",EDGE,"E8.MirrorCS")])]}),"instanceName":"89"});
            var Q90;
            Q90=makeQuery(id+"F8.opExtrude","SWEPT_BODY",BODY,{"disambiguationData":[OSD([sQuery(id+"F4.wireOp",EDGE,"E10")])]});
            booleanBodies(context, id + "F10", {"operationType" : BooleanOperationType.SUBTRACTION, "tools" : qUnion([Q0, Q1, Q2, Q3, Q4, Q5, Q6, Q7, Q8, Q9, Q10, Q11, Q12, Q13, Q14, Q15, Q16, Q17, Q18, Q19, Q20, Q21, Q22, Q23, Q24, Q25, Q26, Q27, Q28, Q29, Q30, Q31, Q32, Q33, Q34, Q35, Q36, Q37, Q38, Q39, Q40, Q41, Q42, Q43, Q44, Q45, Q46, Q47, Q48, Q49, Q50, Q51, Q52, Q53, Q54, Q55, Q56, Q57, Q58, Q59, Q60, Q61, Q62, Q63, Q64, Q65, Q66, Q67, Q68, Q69, Q70, Q71, Q72, Q73, Q74, Q75, Q76, Q77, Q78, Q79, Q80, Q81, Q82, Q83, Q84, Q85, Q86, Q87, Q88, Q89]), "targets" : qUnion([Q90])});
        }
        {
            var Q0;
            Q0=makeQuery(id+"F8.opExtrude","CAP_FACE",FACE,{"disambiguationData":[OSD([sQuery(id+"F4.wireOp",EDGE,"E10")])],"isStart":true});
            var sketch = newSketch(context, id + "F11", { "sketchPlane" : qUnion([Q0])});
            skCircle(sketch, "E12", {"center": v(0, 0) * mm, "radius": 3.17 * mm});
            skCircle(sketch, "E13", {"center": v(0, 0) * mm, "radius": 8.18 * mm});
            skCircle(sketch, "E14", {"center": v(0, 0) * mm, "radius": 25.51 * mm});
            skLineSegment(sketch, "E15", {"start": v(0, 0) * mm, "end": v(0, 25.51) * mm, "construction": true});
            skLineSegment(sketch, "E16.0", {"start": v(2.5, 0) * mm, "end": v(2.5, 25.4) * mm});
            skLineSegment(sketch, "E17", {"start": v(0, 0) * mm, "end": v(30.51, 0) * mm, "construction": true});
            skLineSegment(sketch, "E18.0", {"start": v(0, 2.5) * mm, "end": v(30.41, 2.5) * mm});
            skCircle(sketch, "E19", {"center": v(0, 0) * mm, "radius": 30.51 * mm});
            skSolve(sketch);
        }
        {
            var Q0;
            Q0=makeQuery(id+"F11.imprint","IMPRINT",FACE,{"disambiguationData":[TD([[makeQuery(id+"F11.imprint","IMPRINT",EDGE,{"derivedFrom":sQuery(id+"F11.wireOp",EDGE,"E12")}),1.0]])]});
            extrude(context, id + "F12", {"entities" : qUnion([Q0]), "operationType" : NewBodyOperationType.REMOVE, "oppositeDirection" : true, "depth" : 25 * mm});
        }
        {
            var Q0;
            {var subQ0=sQuery(id+"F11.wireOp",EDGE,"E16.0");var subQ1=sQuery(id+"F11.wireOp",EDGE,"E13");var subQ2=makeQuery(id+"F11.imprint","INTERSECT",VERTEX,{"derivedFrom":[subQ1,subQ0]});Q0=makeQuery(id+"F11.imprint","IMPRINT",FACE,{"disambiguationData":[TD([[makeQuery(id+"F11.imprint","IMPRINT",EDGE,{"disambiguationData":[TD([[subQ2,1.0]])],"derivedFrom":subQ1}),-1.0]])]});}
            extrude(context, id + "F13", {"entities" : qUnion([Q0]), "oppositeDirection" : true, "depth" : 5 * mm, "offsetDistance" : 25 * mm});
        }
        {
            var Q0;
            Q0=makeQuery(id+"F13.opExtrude","SWEPT_BODY",BODY,{"disambiguationData":[OSD([sQuery(id+"F11.wireOp",EDGE,"E13"),sQuery(id+"F11.wireOp",EDGE,"E14"),sQuery(id+"F11.wireOp",EDGE,"E16.0"),sQuery(id+"F11.wireOp",EDGE,"E18.0")])]});
            var Q1;
            Q1=makeQuery(id+"F12.boolean.opBoolean","INTERSECT",EDGE,{"derivedFrom":[makeQuery(id+"F8.opExtrude","CAP_FACE",FACE,{"disambiguationData":[OSD([sQuery(id+"F4.wireOp",EDGE,"E10")])],"isStart":false}),makeQuery(id+"F12.opExtrude","SWEPT_FACE",FACE,{"disambiguationData":[OSD([sQuery(id+"F11.wireOp",EDGE,"E12")])]})]});
            circularPattern(context, id + "F14", {"entities" : qUnion([Q0]), "axis" : qUnion([Q1]), "angle" : 360 * degree, "instanceCount" : getVariable(context, 'SP'), "equalSpace" : true});
        }
        {
            var Q0;
            Q0=makeQuery(id+"F8.opExtrude","CAP_FACE",FACE,{"disambiguationData":[OSD([sQuery(id+"F4.wireOp",EDGE,"E10")])],"isStart":false});
            var sketch = newSketch(context, id + "F15", { "sketchPlane" : qUnion([Q0])});
            skCircle(sketch, "E20", {"center": v(0, 0) * mm, "radius": 8.17 * mm, "construction": true});
            skCircle(sketch, "E21", {"center": v(0, 0) * mm, "radius": 25.51 * mm, "construction": true});
            skLineSegment(sketch, "E22", {"start": v(8.17, 0) * mm, "end": v(25.51, 0) * mm, "construction": true});
            skCircle(sketch, "E23", {"center": v(16.84, 0) * mm, "radius": 2.75 * mm, "construction": true});
            skCircle(sketch, "E24", {"center": v(16.84, 0) * mm, "radius": 7.75 * mm});
            skSolve(sketch);
        }
        {
            var Q0;
            Q0 = qSketchRegion(id + "F15", true);
            extrude(context, id + "F16", {"entities" : qUnion([Q0]), "depth" : -3 * mm, "offsetDistance" : 25 * mm, "hasSecondDirection" : true, "secondDirectionOppositeDirection" : true, "secondDirectionDepth" : -2 * mm});
        }
        {
            var Q0;
            Q0=makeQuery(id+"F16.boolean.opBoolean","MERGE",FACE,{"derivedFrom":[makeQuery(id+"F8.opExtrude","CAP_FACE",FACE,{"disambiguationData":[OSD([sQuery(id+"F4.wireOp",EDGE,"E10")])],"isStart":false}),makeQuery(id+"F16.opExtrude","CAP_FACE",FACE,{"disambiguationData":[OSD([sQuery(id+"F15.wireOp",EDGE,"E24")])],"isStart":true})]});
            var sketch = newSketch(context, id + "F17", { "sketchPlane" : qUnion([Q0])});
            skCircle(sketch, "E25", {"center": v(16.84, 0) * mm, "radius": 2.1 * mm});
            skSolve(sketch);
        }
        {
            var Q0;
            Q0 = qSketchRegion(id + "F17", true);
            extrude(context, id + "F18", {"entities" : qUnion([Q0]), "oppositeDirection" : true, "depth" : 3 * mm, "offsetDistance" : 25 * mm, "hasSecondDirection" : true, "secondDirectionOppositeDirection" : true, "secondDirectionDepth" : -2 * mm});
        }
        {
            var Q0;
            Q0=makeQuery(id+"F16.opExtrude","SWEPT_BODY",BODY,{"disambiguationData":[OSD([sQuery(id+"F15.wireOp",EDGE,"E24")])]});
            var Q1;
            Q1=makeQuery(id+"F18.opExtrude","SWEPT_BODY",BODY,{"disambiguationData":[OSD([sQuery(id+"F17.wireOp",EDGE,"E25")])]});
            var Q2;
            Q2=makeQuery(id+"F12.boolean.opBoolean","INTERSECT",EDGE,{"derivedFrom":[makeQuery(id+"F8.opExtrude","CAP_FACE",FACE,{"disambiguationData":[OSD([sQuery(id+"F4.wireOp",EDGE,"E10")])],"isStart":false}),makeQuery(id+"F12.opExtrude","SWEPT_FACE",FACE,{"disambiguationData":[OSD([sQuery(id+"F11.wireOp",EDGE,"E12")])]})]});
            circularPattern(context, id + "F19", {"entities" : qUnion([Q0, Q1]), "axis" : qUnion([Q2]), "angle" : 360 * degree, "instanceCount" : 2, "equalSpace" : true});
        }
        {
            var Q0;
            Q0=makeQuery(id+"F19.opPattern","COPY",BODY,{"derivedFrom":makeQuery(id+"F16.opExtrude","SWEPT_BODY",BODY,{"disambiguationData":[OSD([sQuery(id+"F15.wireOp",EDGE,"E24")])]}),"instanceName":"1"});
            var Q1;
            Q1=makeQuery(id+"F16.opExtrude","SWEPT_BODY",BODY,{"disambiguationData":[OSD([sQuery(id+"F15.wireOp",EDGE,"E24")])]});
            var Q2;
            Q2=makeQuery(id+"F14.opPattern","COPY",BODY,{"derivedFrom":makeQuery(id+"F13.opExtrude","SWEPT_BODY",BODY,{"disambiguationData":[OSD([sQuery(id+"F11.wireOp",EDGE,"E13"),sQuery(id+"F11.wireOp",EDGE,"E14"),sQuery(id+"F11.wireOp",EDGE,"E16.0"),sQuery(id+"F11.wireOp",EDGE,"E18.0")])]}),"instanceName":"2"});
            var Q3;
            Q3=makeQuery(id+"F14.opPattern","COPY",BODY,{"derivedFrom":makeQuery(id+"F13.opExtrude","SWEPT_BODY",BODY,{"disambiguationData":[OSD([sQuery(id+"F11.wireOp",EDGE,"E13"),sQuery(id+"F11.wireOp",EDGE,"E14"),sQuery(id+"F11.wireOp",EDGE,"E16.0"),sQuery(id+"F11.wireOp",EDGE,"E18.0")])]}),"instanceName":"1"});
            var Q4;
            Q4=makeQuery(id+"F13.opExtrude","SWEPT_BODY",BODY,{"disambiguationData":[OSD([sQuery(id+"F11.wireOp",EDGE,"E13"),sQuery(id+"F11.wireOp",EDGE,"E14"),sQuery(id+"F11.wireOp",EDGE,"E16.0"),sQuery(id+"F11.wireOp",EDGE,"E18.0")])]});
            var Q5;
            Q5=makeQuery(id+"F14.opPattern","COPY",BODY,{"derivedFrom":makeQuery(id+"F13.opExtrude","SWEPT_BODY",BODY,{"disambiguationData":[OSD([sQuery(id+"F11.wireOp",EDGE,"E13"),sQuery(id+"F11.wireOp",EDGE,"E14"),sQuery(id+"F11.wireOp",EDGE,"E16.0"),sQuery(id+"F11.wireOp",EDGE,"E18.0")])]}),"instanceName":"3"});
            booleanBodies(context, id + "F20", {"operationType" : BooleanOperationType.SUBTRACTION, "tools" : qUnion([Q0, Q1]), "targets" : qUnion([Q2, Q3, Q4, Q5])});
        }
        {
            var Q0;
            Q0=makeQuery(id+"F14.opPattern","COPY",FACE,{"derivedFrom":makeQuery(id+"F13.opExtrude","CAP_FACE",FACE,{"disambiguationData":[OSD([sQuery(id+"F11.wireOp",EDGE,"E13"),sQuery(id+"F11.wireOp",EDGE,"E14"),sQuery(id+"F11.wireOp",EDGE,"E16.0"),sQuery(id+"F11.wireOp",EDGE,"E18.0")])],"isStart":false}),"instanceName":"2"});
            var sketch = newSketch(context, id + "F21", { "sketchPlane" : qUnion([Q0])});
            skCircle(sketch, "E26", {"center": v(8.68, 6.2) * mm, "radius": 2.5 * mm});
            skCircle(sketch, "E27", {"center": v(21.03, 9.36) * mm, "radius": 2.5 * mm});
            skCircle(sketch, "E28", {"center": v(0, 0) * mm, "radius": 8.18 * mm});
            skCircle(sketch, "E29", {"center": v(0, 0) * mm, "radius": 25.51 * mm});
            skCircle(sketch, "E30", {"center": v(16.84, 0) * mm, "radius": 7.75 * mm});
            skLineSegment(sketch, "E31", {"start": v(0, 0) * mm, "end": v(25.51, 0) * mm, "construction": true});
            skLineSegment(sketch, "E32", {"start": v(5.16, 2.5) * mm, "end": v(26.6, 2.5) * mm});
            skSolve(sketch);
        }
        {
            var Q0;
            {var subQ0=sQuery(id+"F21.wireOp",EDGE,"E29");var subQ1=sQuery(id+"F21.wireOp",EDGE,"E27");var subQ2=makeQuery(id+"F21.imprint","INTERSECT",VERTEX,{"derivedFrom":[subQ1,subQ0]});Q0=makeQuery(id+"F21.imprint","IMPRINT",FACE,{"disambiguationData":[TD([[makeQuery(id+"F21.imprint","IMPRINT",EDGE,{"disambiguationData":[TD([[subQ2,1.0]])],"derivedFrom":subQ1}),-1.0]])]});}
            var Q1;
            {var subQ0=sQuery(id+"F21.wireOp",EDGE,"E28");var subQ1=sQuery(id+"F21.wireOp",EDGE,"E26");var subQ2=makeQuery(id+"F21.imprint","INTERSECT",VERTEX,{"derivedFrom":[subQ1,subQ0]});Q1=makeQuery(id+"F21.imprint","IMPRINT",FACE,{"disambiguationData":[TD([[makeQuery(id+"F21.imprint","IMPRINT",EDGE,{"disambiguationData":[TD([[subQ2,-1.0]])],"derivedFrom":subQ1}),-1.0]])]});}
            extrude(context, id + "F22", {"entities" : qUnion([Q0, Q1]), "depth" : -5 * mm, "offsetDistance" : 25 * mm});
        }
        {
            var Q0;
            Q0=makeQuery(id+"F22.opExtrude","SWEPT_BODY",BODY,{"disambiguationData":[OSD([sQuery(id+"F21.wireOp",EDGE,"E27"),sQuery(id+"F21.wireOp",EDGE,"E29"),sQuery(id+"F21.wireOp",EDGE,"E30"),sQuery(id+"F21.wireOp",EDGE,"E32")])]});
            var Q1;
            Q1=makeQuery(id+"F22.opExtrude","SWEPT_BODY",BODY,{"disambiguationData":[OSD([sQuery(id+"F21.wireOp",EDGE,"E26"),sQuery(id+"F21.wireOp",EDGE,"E28"),sQuery(id+"F21.wireOp",EDGE,"E30"),sQuery(id+"F21.wireOp",EDGE,"E32")])]});
            var Q2;
            Q2=qCreatedBy(makeId("Front.planeOp"),FACE);
            mirror(context, id + "F23", {"entities" : qUnion([Q0, Q1]), "mirrorPlane" : qUnion([Q2])});
        }
        {
            var Q0;
            Q0=makeQuery(id+"F22.opExtrude","SWEPT_BODY",BODY,{"disambiguationData":[OSD([sQuery(id+"F21.wireOp",EDGE,"E27"),sQuery(id+"F21.wireOp",EDGE,"E29"),sQuery(id+"F21.wireOp",EDGE,"E30"),sQuery(id+"F21.wireOp",EDGE,"E32")])]});
            var Q1;
            Q1=makeQuery(id+"F22.opExtrude","SWEPT_BODY",BODY,{"disambiguationData":[OSD([sQuery(id+"F21.wireOp",EDGE,"E26"),sQuery(id+"F21.wireOp",EDGE,"E28"),sQuery(id+"F21.wireOp",EDGE,"E30"),sQuery(id+"F21.wireOp",EDGE,"E32")])]});
            var Q2;
            Q2=makeQuery(id+"F23.opPattern","COPY",BODY,{"derivedFrom":makeQuery(id+"F22.opExtrude","SWEPT_BODY",BODY,{"disambiguationData":[OSD([sQuery(id+"F21.wireOp",EDGE,"E26"),sQuery(id+"F21.wireOp",EDGE,"E28"),sQuery(id+"F21.wireOp",EDGE,"E30"),sQuery(id+"F21.wireOp",EDGE,"E32")])]}),"instanceName":"1"});
            var Q3;
            Q3=makeQuery(id+"F23.opPattern","COPY",BODY,{"derivedFrom":makeQuery(id+"F22.opExtrude","SWEPT_BODY",BODY,{"disambiguationData":[OSD([sQuery(id+"F21.wireOp",EDGE,"E27"),sQuery(id+"F21.wireOp",EDGE,"E29"),sQuery(id+"F21.wireOp",EDGE,"E30"),sQuery(id+"F21.wireOp",EDGE,"E32")])]}),"instanceName":"1"});
            var Q4;
            Q4=qCreatedBy(makeId("Right.planeOp"),FACE);
            mirror(context, id + "F24", {"entities" : qUnion([Q0, Q1, Q2, Q3]), "mirrorPlane" : qUnion([Q4])});
        }
        {
            var Q0;
            Q0=makeQuery(id+"F24.opPattern","COPY",BODY,{"derivedFrom":makeQuery(id+"F22.opExtrude","SWEPT_BODY",BODY,{"disambiguationData":[OSD([sQuery(id+"F21.wireOp",EDGE,"E26"),sQuery(id+"F21.wireOp",EDGE,"E28"),sQuery(id+"F21.wireOp",EDGE,"E30"),sQuery(id+"F21.wireOp",EDGE,"E32")])]}),"instanceName":"1"});
            var Q1;
            Q1=makeQuery(id+"F24.opPattern","COPY",BODY,{"derivedFrom":makeQuery(id+"F22.opExtrude","SWEPT_BODY",BODY,{"disambiguationData":[OSD([sQuery(id+"F21.wireOp",EDGE,"E27"),sQuery(id+"F21.wireOp",EDGE,"E29"),sQuery(id+"F21.wireOp",EDGE,"E30"),sQuery(id+"F21.wireOp",EDGE,"E32")])]}),"instanceName":"1"});
            var Q2;
            Q2=makeQuery(id+"F24.opPattern","COPY",BODY,{"derivedFrom":makeQuery(id+"F23.opPattern","COPY",BODY,{"derivedFrom":makeQuery(id+"F22.opExtrude","SWEPT_BODY",BODY,{"disambiguationData":[OSD([sQuery(id+"F21.wireOp",EDGE,"E27"),sQuery(id+"F21.wireOp",EDGE,"E29"),sQuery(id+"F21.wireOp",EDGE,"E30"),sQuery(id+"F21.wireOp",EDGE,"E32")])]}),"instanceName":"1"}),"instanceName":"1"});
            var Q3;
            Q3=makeQuery(id+"F24.opPattern","COPY",BODY,{"derivedFrom":makeQuery(id+"F23.opPattern","COPY",BODY,{"derivedFrom":makeQuery(id+"F22.opExtrude","SWEPT_BODY",BODY,{"disambiguationData":[OSD([sQuery(id+"F21.wireOp",EDGE,"E26"),sQuery(id+"F21.wireOp",EDGE,"E28"),sQuery(id+"F21.wireOp",EDGE,"E30"),sQuery(id+"F21.wireOp",EDGE,"E32")])]}),"instanceName":"1"}),"instanceName":"1"});
            var Q4;
            Q4=makeQuery(id+"F23.opPattern","COPY",BODY,{"derivedFrom":makeQuery(id+"F22.opExtrude","SWEPT_BODY",BODY,{"disambiguationData":[OSD([sQuery(id+"F21.wireOp",EDGE,"E26"),sQuery(id+"F21.wireOp",EDGE,"E28"),sQuery(id+"F21.wireOp",EDGE,"E30"),sQuery(id+"F21.wireOp",EDGE,"E32")])]}),"instanceName":"1"});
            var Q5;
            Q5=makeQuery(id+"F22.opExtrude","SWEPT_BODY",BODY,{"disambiguationData":[OSD([sQuery(id+"F21.wireOp",EDGE,"E26"),sQuery(id+"F21.wireOp",EDGE,"E28"),sQuery(id+"F21.wireOp",EDGE,"E30"),sQuery(id+"F21.wireOp",EDGE,"E32")])]});
            var Q6;
            Q6=makeQuery(id+"F22.opExtrude","SWEPT_BODY",BODY,{"disambiguationData":[OSD([sQuery(id+"F21.wireOp",EDGE,"E27"),sQuery(id+"F21.wireOp",EDGE,"E29"),sQuery(id+"F21.wireOp",EDGE,"E30"),sQuery(id+"F21.wireOp",EDGE,"E32")])]});
            var Q7;
            Q7=makeQuery(id+"F23.opPattern","COPY",BODY,{"derivedFrom":makeQuery(id+"F22.opExtrude","SWEPT_BODY",BODY,{"disambiguationData":[OSD([sQuery(id+"F21.wireOp",EDGE,"E27"),sQuery(id+"F21.wireOp",EDGE,"E29"),sQuery(id+"F21.wireOp",EDGE,"E30"),sQuery(id+"F21.wireOp",EDGE,"E32")])]}),"instanceName":"1"});
            var Q8;
            Q8=makeQuery(id+"F14.opPattern","COPY",BODY,{"derivedFrom":makeQuery(id+"F13.opExtrude","SWEPT_BODY",BODY,{"disambiguationData":[OSD([sQuery(id+"F11.wireOp",EDGE,"E13"),sQuery(id+"F11.wireOp",EDGE,"E14"),sQuery(id+"F11.wireOp",EDGE,"E16.0"),sQuery(id+"F11.wireOp",EDGE,"E18.0")])]}),"instanceName":"2"});
            var Q9;
            Q9=makeQuery(id+"F14.opPattern","COPY",BODY,{"derivedFrom":makeQuery(id+"F13.opExtrude","SWEPT_BODY",BODY,{"disambiguationData":[OSD([sQuery(id+"F11.wireOp",EDGE,"E13"),sQuery(id+"F11.wireOp",EDGE,"E14"),sQuery(id+"F11.wireOp",EDGE,"E16.0"),sQuery(id+"F11.wireOp",EDGE,"E18.0")])]}),"instanceName":"1"});
            var Q10;
            Q10=makeQuery(id+"F13.opExtrude","SWEPT_BODY",BODY,{"disambiguationData":[OSD([sQuery(id+"F11.wireOp",EDGE,"E13"),sQuery(id+"F11.wireOp",EDGE,"E14"),sQuery(id+"F11.wireOp",EDGE,"E16.0"),sQuery(id+"F11.wireOp",EDGE,"E18.0")])]});
            var Q11;
            Q11=makeQuery(id+"F14.opPattern","COPY",BODY,{"derivedFrom":makeQuery(id+"F13.opExtrude","SWEPT_BODY",BODY,{"disambiguationData":[OSD([sQuery(id+"F11.wireOp",EDGE,"E13"),sQuery(id+"F11.wireOp",EDGE,"E14"),sQuery(id+"F11.wireOp",EDGE,"E16.0"),sQuery(id+"F11.wireOp",EDGE,"E18.0")])]}),"instanceName":"3"});
            booleanBodies(context, id + "F25", {"operationType" : BooleanOperationType.SUBTRACTION, "tools" : qUnion([Q0, Q1, Q2, Q3, Q4, Q5, Q6, Q7]), "targets" : qUnion([Q8, Q9, Q10, Q11])});
        }
        {
            var Q0;
            Q0=makeQuery(id+"F14.opPattern","COPY",EDGE,{"derivedFrom":makeQuery(id+"F13.opExtrude","SWEPT_EDGE",EDGE,{"disambiguationData":[OSD([sQuery(id+"F11.wireOp",EDGE,"E14"),sQuery(id+"F11.wireOp",EDGE,"E18.0")])]}),"instanceName":"3"});
            var Q1;
            Q1=makeQuery(id+"F14.opPattern","COPY",EDGE,{"derivedFrom":makeQuery(id+"F13.opExtrude","SWEPT_EDGE",EDGE,{"disambiguationData":[OSD([sQuery(id+"F11.wireOp",EDGE,"E13"),sQuery(id+"F11.wireOp",EDGE,"E16.0")])]}),"instanceName":"2"});
            var Q2;
            Q2=makeQuery(id+"F14.opPattern","COPY",EDGE,{"derivedFrom":makeQuery(id+"F13.opExtrude","SWEPT_EDGE",EDGE,{"disambiguationData":[OSD([sQuery(id+"F11.wireOp",EDGE,"E13"),sQuery(id+"F11.wireOp",EDGE,"E18.0")])]}),"instanceName":"1"});
            var Q3;
            Q3=makeQuery(id+"F13.opExtrude","SWEPT_EDGE",EDGE,{"disambiguationData":[OSD([sQuery(id+"F11.wireOp",EDGE,"E14"),sQuery(id+"F11.wireOp",EDGE,"E16.0")])]});
            var Q4;
            Q4=makeQuery(id+"F13.opExtrude","SWEPT_EDGE",EDGE,{"disambiguationData":[OSD([sQuery(id+"F11.wireOp",EDGE,"E13"),sQuery(id+"F11.wireOp",EDGE,"E16.0")])]});
            var Q5;
            Q5=makeQuery(id+"F14.opPattern","COPY",EDGE,{"derivedFrom":makeQuery(id+"F13.opExtrude","SWEPT_EDGE",EDGE,{"disambiguationData":[OSD([sQuery(id+"F11.wireOp",EDGE,"E13"),sQuery(id+"F11.wireOp",EDGE,"E18.0")])]}),"instanceName":"3"});
            var Q6;
            Q6=makeQuery(id+"F14.opPattern","COPY",EDGE,{"derivedFrom":makeQuery(id+"F13.opExtrude","SWEPT_EDGE",EDGE,{"disambiguationData":[OSD([sQuery(id+"F11.wireOp",EDGE,"E14"),sQuery(id+"F11.wireOp",EDGE,"E16.0")])]}),"instanceName":"2"});
            var Q7;
            Q7=makeQuery(id+"F14.opPattern","COPY",EDGE,{"derivedFrom":makeQuery(id+"F13.opExtrude","SWEPT_EDGE",EDGE,{"disambiguationData":[OSD([sQuery(id+"F11.wireOp",EDGE,"E14"),sQuery(id+"F11.wireOp",EDGE,"E18.0")])]}),"instanceName":"1"});
            fillet(context, id + "F26", {"entities" : qUnion([Q0, Q1, Q2, Q3, Q4, Q5, Q6, Q7]), "radius" : (getVariable(context, 'SF')) * mm, "tangentPropagation" : true, "allowEdgeOverflow" : false});
        }
        {
            var Q0;
            Q0=makeQuery(id+"F14.opPattern","COPY",BODY,{"derivedFrom":makeQuery(id+"F13.opExtrude","SWEPT_BODY",BODY,{"disambiguationData":[OSD([sQuery(id+"F11.wireOp",EDGE,"E13"),sQuery(id+"F11.wireOp",EDGE,"E14"),sQuery(id+"F11.wireOp",EDGE,"E16.0"),sQuery(id+"F11.wireOp",EDGE,"E18.0")])]}),"instanceName":"2"});
            var Q1;
            Q1=makeQuery(id+"F19.opPattern","COPY",BODY,{"derivedFrom":makeQuery(id+"F18.opExtrude","SWEPT_BODY",BODY,{"disambiguationData":[OSD([sQuery(id+"F17.wireOp",EDGE,"E25")])]}),"instanceName":"1"});
            var Q2;
            Q2=makeQuery(id+"F14.opPattern","COPY",BODY,{"derivedFrom":makeQuery(id+"F13.opExtrude","SWEPT_BODY",BODY,{"disambiguationData":[OSD([sQuery(id+"F11.wireOp",EDGE,"E13"),sQuery(id+"F11.wireOp",EDGE,"E14"),sQuery(id+"F11.wireOp",EDGE,"E16.0"),sQuery(id+"F11.wireOp",EDGE,"E18.0")])]}),"instanceName":"3"});
            var Q3;
            Q3=makeQuery(id+"F13.opExtrude","SWEPT_BODY",BODY,{"disambiguationData":[OSD([sQuery(id+"F11.wireOp",EDGE,"E13"),sQuery(id+"F11.wireOp",EDGE,"E14"),sQuery(id+"F11.wireOp",EDGE,"E16.0"),sQuery(id+"F11.wireOp",EDGE,"E18.0")])]});
            var Q4;
            Q4=makeQuery(id+"F18.opExtrude","SWEPT_BODY",BODY,{"disambiguationData":[OSD([sQuery(id+"F17.wireOp",EDGE,"E25")])]});
            var Q5;
            Q5=makeQuery(id+"F14.opPattern","COPY",BODY,{"derivedFrom":makeQuery(id+"F13.opExtrude","SWEPT_BODY",BODY,{"disambiguationData":[OSD([sQuery(id+"F11.wireOp",EDGE,"E13"),sQuery(id+"F11.wireOp",EDGE,"E14"),sQuery(id+"F11.wireOp",EDGE,"E16.0"),sQuery(id+"F11.wireOp",EDGE,"E18.0")])]}),"instanceName":"1"});
            var Q6;
            Q6=makeQuery(id+"F8.opExtrude","SWEPT_BODY",BODY,{"disambiguationData":[OSD([sQuery(id+"F4.wireOp",EDGE,"E10")])]});
            booleanBodies(context, id + "F27", {"operationType" : BooleanOperationType.SUBTRACTION, "tools" : qUnion([Q0, Q1, Q2, Q3, Q4, Q5]), "targets" : qUnion([Q6])});
        }
    });
